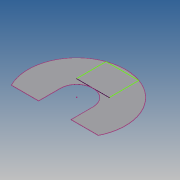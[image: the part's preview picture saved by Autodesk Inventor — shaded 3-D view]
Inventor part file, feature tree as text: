
AUTODESK INVENTOR PART (.ipt)
format: ipt  version: 2013 (Build 170138000, 138)  size: 82,944 bytes
history: native  units: mm
features: sketch x2, extrude x1
ambient origin geometry x8: Origin, YZ Plane, XZ Plane, XY Plane, X Axis, Y Axis, Z Axis, Center Point
bodies: Solid1 (feature_tree)
feature tree (3):
  extrude  "Extrusion1"  Depth=600.0mm
  sketch  "Sketch2"  dims[d3=135.0mm d7=3.0mm d8=0.0mm]
  sketch  "Sketch1"  dims[d0=200.0mm d2=600.0mm]
